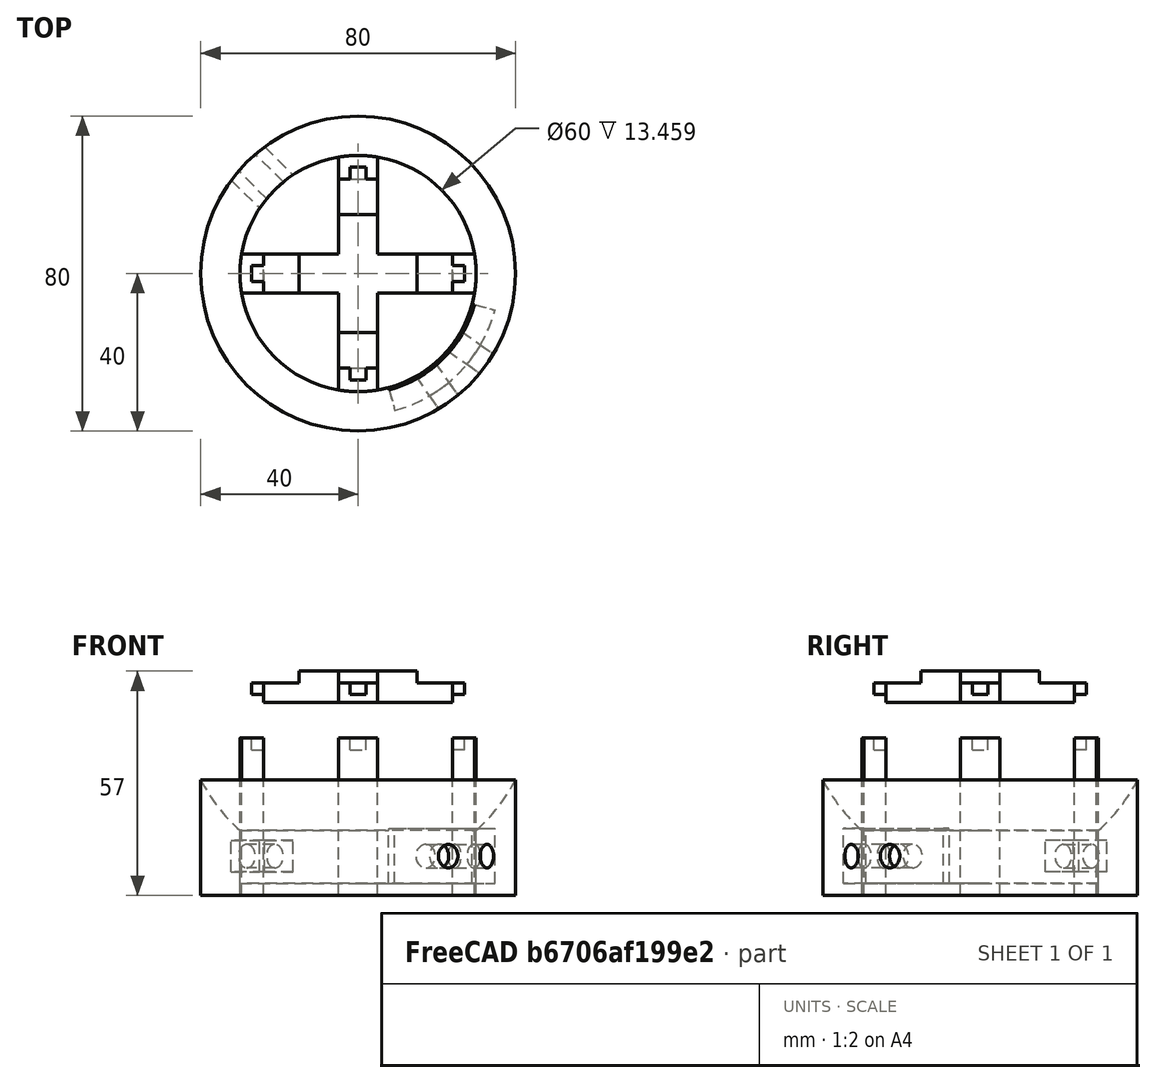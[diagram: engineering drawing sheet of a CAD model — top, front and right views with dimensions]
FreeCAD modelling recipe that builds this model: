
FCSTD DOCUMENT  (FreeCAD 0.16RUnknown)
Label: DerMondEinStroboskop
License: All rights reserved
LicenseURL: http://en.wikipedia.org/wiki/All_rights_reserved
objects: Part::Box×17, Part::Cut×14, Part::Cylinder×8, Part::MultiCommon×4, Part::MultiFuse×3, Part::Sphere×1
note: 47 computed .brp shape members not serialized (recipe doc carries the construction recipe); baked Part::Feature solids carry a one-line shape summary decoded from their .brp

FEATURE [Part::Cylinder] Cylinder
  Angle = 360
  Height = 30
  Radius = 40
FEATURE [Part::Cylinder] Cylinder001
  Angle = 360
  Height = 30
  Placement = pos=(0,0,3) rot=(0,0,1;0rad)
  Radius = 30
FEATURE [Part::Sphere] Sphere
  Angle1 = -90
  Angle2 = 90
  Angle3 = 360
  Placement = pos=(0,0,50) rot=(0,0,1;0rad)
  Radius = 45
FEATURE [Part::Cut] Cut
  Base = -> Cylinder
  Tool = -> Cylinder001
FEATURE [Part::Cut] Cut001
  Base = -> Cut
  Tool = -> Sphere
FEATURE [Part::Cylinder] Cylinder002  label="switch1"
  Angle = 360
  Height = 12
  Placement = pos=(16.6337,-23.7554,10) rot=(0.419215,0.805305,-0.419215;1.78566rad)
  Radius = 3
FEATURE [Part::Cylinder] Cylinder003  label="switch2"
  Angle = 360
  Height = 12
  Placement = pos=(23.7554,-16.6337,10) rot=(0.287968,0.913318,-0.287968;1.66134rad)
  Radius = 3
FEATURE [Part::Cylinder] Cylinder004  label="plug"
  Angle = 360
  Height = 12
  Placement = pos=(-20.5061,20.5061,10) rot=(-0.678598,0.281085,0.678598;2.59356rad)
  Radius = 3
FEATURE [Part::Cut] Cut002
  Base = -> Cut001
  Tool = -> Cylinder004
FEATURE [Part::Cut] Cut003
  Base = -> Cut002
  Tool = -> Cylinder002
FEATURE [Part::Cut] Cut004  label="base_round"
  Base = -> Cut003
  Tool = -> Cylinder003
FEATURE [Part::Box] Box  label="Cube"
  Height = 45
  Length = 6
  Width = 10
FEATURE [Part::Box] Box001  label="Cube001"
  Height = 10
  Length = 10
  Placement = pos=(3,3,42) rot=(0,0,1;0rad)
  Width = 4
FEATURE [Part::Cut] Cut005
  Base = -> Box
  Placement = pos=(-30,-5,-5) rot=(0,0,1;0rad)
  Tool = -> Box001
FEATURE [Part::Box] Box002  label="Cube002"
  Height = 45
  Length = 6
  Width = 10
FEATURE [Part::Box] Box003  label="Cube003"
  Height = 10
  Length = 10
  Placement = pos=(3,3,42) rot=(0,0,1;0rad)
  Width = 4
FEATURE [Part::Cut] Cut006
  Base = -> Box002
  Placement = pos=(5,-30,-5) rot=(0,0,1;1.5708rad)
  Tool = -> Box003
FEATURE [Part::Box] Box004  label="Cube004"
  Height = 45
  Length = 6
  Width = 10
FEATURE [Part::Box] Box005  label="Cube005"
  Height = 10
  Length = 10
  Placement = pos=(3,3,42) rot=(0,0,1;0rad)
  Width = 4
FEATURE [Part::Cut] Cut007
  Base = -> Box004
  Placement = pos=(-5,30,-5) rot=(0,0,-1;1.5708rad)
  Tool = -> Box005
FEATURE [Part::Box] Box006  label="Cube006"
  Height = 45
  Length = 6
  Width = 10
FEATURE [Part::Box] Box007  label="Cube007"
  Height = 10
  Length = 10
  Placement = pos=(3,3,42) rot=(0,0,1;0rad)
  Width = 4
FEATURE [Part::Cut] Cut008
  Base = -> Box006
  Placement = pos=(30,5,-5) rot=(0,0,1;3.14159rad)
  Tool = -> Box007
FEATURE [Part::Cylinder] Cylinder005  label="Cylinder002"
  Angle = 360
  Height = 40
  Radius = 30
FEATURE [Part::MultiCommon] Common  label="snap1"
  Shapes = -> [Cylinder005,Cut008]
FEATURE [Part::MultiCommon] Common001  label="snap2"
  Shapes = -> [Cut006,Cylinder005]
FEATURE [Part::MultiCommon] Common002  label="snap3"
  Shapes = -> [Cut005,Cylinder005]
FEATURE [Part::MultiCommon] Common003  label="snap4"
  Shapes = -> [Cut007,Cylinder005]
FEATURE [Part::Cut] Cut009
  Base = -> Cut001
  Tool = -> Cylinder002
FEATURE [Part::Cut] Cut010
  Base = -> Cut009
  Tool = -> Cylinder003
FEATURE [Part::Box] Box008  label="Cube008"
  Height = 8
  Length = 12
  Placement = pos=(-33.234,24.7487,6) rot=(0,0,-1;0.785398rad)
  Width = 12
FEATURE [Part::Cut] Cut011  label="base"
  Base = -> Cut010
  Tool = -> Box008
FEATURE [Part::Box] Box009  label="Cube009"
  Height = 10
  Length = 48
  Placement = pos=(-24,-5,30) rot=(0,0,1;0rad)
  Width = 10
FEATURE [Part::Box] Box010  label="Cube010"
  Height = 3
  Length = 3
  Placement = pos=(-27,-2,37) rot=(0,0,1;0rad)
  Width = 4
FEATURE [Part::Box] Box011  label="Cube011"
  Height = 3
  Length = 3
  Placement = pos=(24,-2,37) rot=(0,0,1;0rad)
  Width = 4
FEATURE [Part::Box] Box012  label="Cube012"
  Height = 10
  Length = 10
  Placement = pos=(-5,-24,30) rot=(0,0,1;0rad)
  Width = 48
FEATURE [Part::Box] Box013  label="Cube013"
  Height = 3
  Length = 4
  Placement = pos=(-2,24,37) rot=(0,0,1;0rad)
  Width = 3
FEATURE [Part::Box] Box014  label="Cube014"
  Height = 3
  Length = 4
  Placement = pos=(-2,-27,37) rot=(0,0,1;0rad)
  Width = 3
FEATURE [Part::Box] Box015  label="Cube015"
  Height = 10
  Length = 30
  Placement = pos=(-15,-5,33) rot=(0,0,1;0rad)
  Width = 10
FEATURE [Part::Box] Box016  label="Cube016"
  Height = 10
  Length = 10
  Placement = pos=(-5,-15,33) rot=(0,0,1;0rad)
  Width = 30
FEATURE [Part::MultiFuse] Fusion
  Shapes = -> [Box009,Box010,Box011,Box015]
FEATURE [Part::MultiFuse] Fusion001
  Shapes = -> [Box016,Box013,Box012,Box014]
FEATURE [Part::MultiFuse] Fusion002
  Placement = pos=(0,0,14) rot=(0,0,1;0rad)
  Shapes = -> [Fusion001,Fusion]
FEATURE [Part::Cylinder] Cylinder006  label="Cylinder003"
  Angle = 360
  Height = 20
  Placement = pos=(0,0,29) rot=(0,0,1;0rad)
  Radius = 40
FEATURE [Part::Cut] Cut012  label="LED"
  Base = -> Fusion002
  Tool = -> Cylinder006
FEATURE [Part::Cylinder] Cylinder007  label="Cylinder004"
  Angle = 60
  Height = 14
  Placement = pos=(0,0,3) rot=(0,0,-1;1.309rad)
  Radius = 36
FEATURE [Part::Cut] Cut013
  Base = -> Cut011
  Tool = -> Cylinder007
